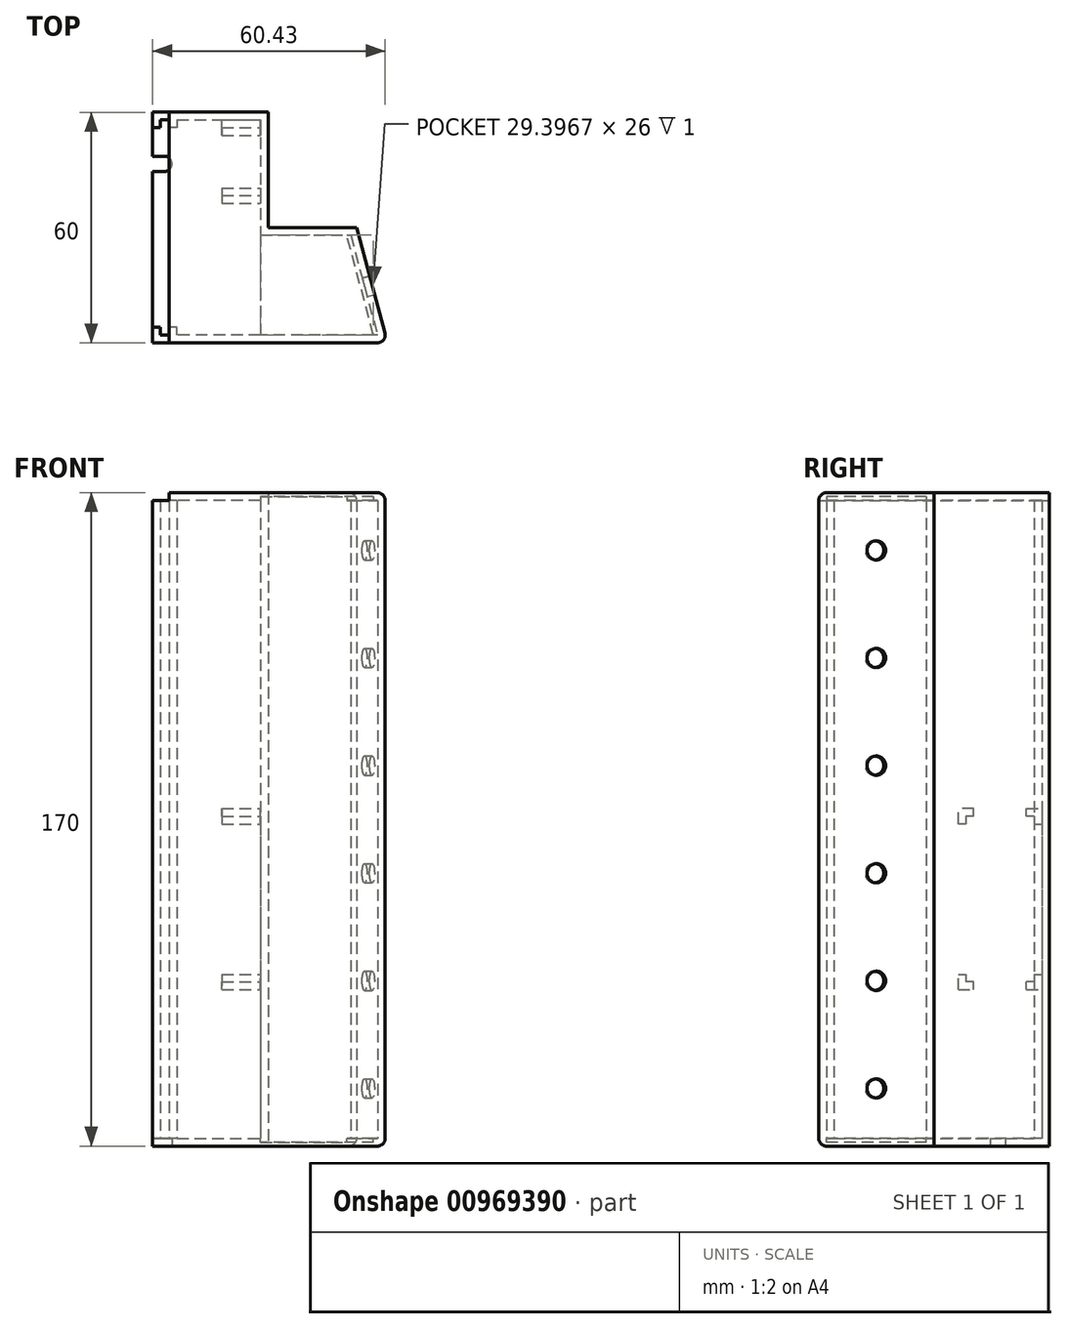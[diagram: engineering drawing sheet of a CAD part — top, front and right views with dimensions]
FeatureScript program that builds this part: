
annotation { "Feature Type Name" : "Feature", "Feature Type Description" : "" }
export const myFeature = defineFeature(function(context is Context, id is Id, definition is map)
    precondition{}
    {
        {
            var Q0;
            Q0=qCreatedBy(makeId("Top.planeOp"),FACE);
            var sketch = newSketch(context, id + "F0", { "sketchPlane" : qUnion([Q0])});
            skLineSegment(sketch, "E0.bottom", {"start": v(18.2, -39.79) * mm, "end": v(-42.84, -39.79) * mm});
            skLineSegment(sketch, "E0.right", {"start": v(-42.84, -39.79) * mm, "end": v(-42.84, -9.79) * mm});
            skLineSegment(sketch, "E1.top", {"start": v(-42.84, 20.21) * mm, "end": v(-12.84, 20.21) * mm});
            skLineSegment(sketch, "E1.left", {"start": v(-42.84, -9.79) * mm, "end": v(-42.84, 20.21) * mm});
            skLineSegment(sketch, "E1.right", {"start": v(-12.84, -9.79) * mm, "end": v(-12.84, 20.21) * mm});
            skLineSegment(sketch, "E2", {"start": v(10.16, -9.79) * mm, "end": v(18.2, -39.79) * mm});
            skLineSegment(sketch, "E3", {"start": v(10.16, -9.79) * mm, "end": v(10.16, -39.79) * mm, "construction": true});
            skLineSegment(sketch, "E4", {"start": v(-12.84, -9.79) * mm, "end": v(10.16, -9.79) * mm});
            skSolve(sketch);
        }
        {
            var Q0;
            Q0=makeQuery(id+"F0.imprint","IMPRINT",FACE,{"disambiguationData":[TD([[makeQuery(id+"F0.imprint","IMPRINT",EDGE,{"derivedFrom":sQuery(id+"F0.wireOp",EDGE,"E0.bottom")}),-1.0]])]});
            extrude(context, id + "F1", {"entities" : qUnion([Q0]), "depth" : 2 * mm, "offsetDistance" : 25 * mm});
        }
        {
            var Q0;
            Q0=makeQuery(id+"F1.opExtrude","CAP_FACE",FACE,{"disambiguationData":[OSD([sQuery(id+"F0.wireOp",EDGE,"E0.bottom"),sQuery(id+"F0.wireOp",EDGE,"E0.right"),sQuery(id+"F0.wireOp",EDGE,"E1.top"),sQuery(id+"F0.wireOp",EDGE,"E1.left"),sQuery(id+"F0.wireOp",EDGE,"E1.right"),sQuery(id+"F0.wireOp",EDGE,"E2"),sQuery(id+"F0.wireOp",EDGE,"E4")])],"isStart":false});
            var sketch = newSketch(context, id + "F2", { "sketchPlane" : qUnion([Q0])});
            skLineSegment(sketch, "E5", {"start": v(-36.54, 18.21) * mm, "end": v(-14.84, 18.21) * mm});
            skLineSegment(sketch, "E6", {"start": v(-14.84, 18.21) * mm, "end": v(-14.84, -11.79) * mm});
            skLineSegment(sketch, "E7", {"start": v(-14.84, -11.79) * mm, "end": v(8.63, -11.79) * mm});
            skLineSegment(sketch, "E8", {"start": v(8.63, -11.79) * mm, "end": v(15.6, -37.79) * mm});
            skLineSegment(sketch, "E9", {"start": v(15.6, -37.79) * mm, "end": v(-36.54, -37.79) * mm});
            skLineSegment(sketch, "E10", {"start": v(-36.54, 18.21) * mm, "end": v(-36.54, 16.21) * mm});
            skLineSegment(sketch, "E11", {"start": v(-36.54, 16.21) * mm, "end": v(-38.54, 16.21) * mm});
            skLineSegment(sketch, "E12", {"start": v(-38.54, 16.21) * mm, "end": v(-38.54, 18.21) * mm});
            skLineSegment(sketch, "E13", {"start": v(-38.54, 18.21) * mm, "end": v(-40.84, 18.21) * mm});
            skLineSegment(sketch, "E14", {"start": v(-40.84, 18.21) * mm, "end": v(-40.84, 16.21) * mm});
            skLineSegment(sketch, "E15", {"start": v(-40.84, 16.21) * mm, "end": v(-42.84, 16.21) * mm});
            skLineSegment(sketch, "E16", {"start": v(-36.54, -37.79) * mm, "end": v(-36.54, -35.79) * mm});
            skLineSegment(sketch, "E17", {"start": v(-36.54, -35.79) * mm, "end": v(-38.54, -35.79) * mm});
            skLineSegment(sketch, "E18", {"start": v(-38.54, -35.79) * mm, "end": v(-38.54, -37.79) * mm});
            skLineSegment(sketch, "E19", {"start": v(-38.54, -37.79) * mm, "end": v(-40.84, -37.79) * mm});
            skLineSegment(sketch, "E20", {"start": v(-40.84, -37.79) * mm, "end": v(-40.84, -35.79) * mm});
            skLineSegment(sketch, "E21", {"start": v(-40.84, -35.79) * mm, "end": v(-42.84, -35.79) * mm});
            skSolve(sketch);
        }
        {
            var Q0;
            Q0=makeQuery(id+"F2.imprint","IMPRINT",FACE,{"disambiguationData":[TD([[makeQuery(id+"F2.imprint","IMPRINT",EDGE,{"derivedFrom":sQuery(id+"F2.wireOp",EDGE,"E5")}),1.0]])]});
            extrude(context, id + "F3", {"entities" : qUnion([Q0]), "operationType" : NewBodyOperationType.ADD, "depth" : 166 * mm, "offsetDistance" : 25 * mm});
        }
        {
            var Q0;
            {var subQ0=sQuery(id+"F0.wireOp",EDGE,"E2");Q0=makeQuery(id+"F3.boolean.opBoolean","MERGE",FACE,{"derivedFrom":[makeQuery(id+"F1.opExtrude","SWEPT_FACE",FACE,{"disambiguationData":[OSD([subQ0])]}),makeQuery(id+"F3.opExtrude","SWEPT_FACE",FACE,{"disambiguationData":[OSD([subQ0])]})]});}
            var sketch = newSketch(context, id + "F4", { "sketchPlane" : qUnion([Q0])});
            skLineSegment(sketch, "E22", {"start": v(-27.61, 168) * mm, "end": v(-27.61, 0) * mm, "construction": true});
            skPoint(sketch, "E23", {"position": v(-27.61, 155) * mm});
            skPoint(sketch, "E24", {"position": v(-27.61, 127) * mm});
            skPoint(sketch, "E25", {"position": v(-27.61, 99) * mm});
            skPoint(sketch, "E26", {"position": v(-27.61, 71) * mm});
            skPoint(sketch, "E27", {"position": v(-27.61, 43) * mm});
            skPoint(sketch, "E28", {"position": v(-27.61, 15) * mm});
            skSolve(sketch);
        }
        {
            var Q0;
            Q0=sQuery(id+"F4.wireOp",VERTEX,"E23");
            var Q1;
            Q1=sQuery(id+"F4.wireOp",VERTEX,"E24");
            var Q2;
            Q2=sQuery(id+"F4.wireOp",VERTEX,"E25");
            var Q3;
            Q3=sQuery(id+"F4.wireOp",VERTEX,"E26");
            var Q4;
            Q4=sQuery(id+"F4.wireOp",VERTEX,"E27");
            var Q5;
            Q5=sQuery(id+"F4.wireOp",VERTEX,"E28");
            var Q6;
            Q6=makeQuery(id+"F1.opExtrude","SWEPT_BODY",BODY,{"disambiguationData":[OSD([sQuery(id+"F0.wireOp",EDGE,"E0.bottom"),sQuery(id+"F0.wireOp",EDGE,"E0.right"),sQuery(id+"F0.wireOp",EDGE,"E1.top"),sQuery(id+"F0.wireOp",EDGE,"E1.left"),sQuery(id+"F0.wireOp",EDGE,"E1.right"),sQuery(id+"F0.wireOp",EDGE,"E2"),sQuery(id+"F0.wireOp",EDGE,"E4")])]});
            hole(context, id + "F5", {"style" : HoleStyle.SIMPLE, "endStyle" : HoleEndStyle.BLIND, "holeDiameter" : 5 * mm, "majorDiameter" : 5 * mm, "holeDepth" : 10 * mm, "isTappedThrough" : true, "tappedDepth" : 12 * mm, "tapClearance" : 3, "locations" : qUnion([Q0, Q1, Q2, Q3, Q4, Q5]), "scope" : qUnion([Q6])});
        }
        {
            var Q0;
            Q0=makeQuery(id+"F3.opExtrude","CAP_FACE",FACE,{"disambiguationData":[OSD([sQuery(id+"F0.wireOp",EDGE,"E0.bottom"),sQuery(id+"F0.wireOp",EDGE,"E0.right"),sQuery(id+"F0.wireOp",EDGE,"E1.top"),sQuery(id+"F0.wireOp",EDGE,"E1.left"),sQuery(id+"F0.wireOp",EDGE,"E1.right"),sQuery(id+"F0.wireOp",EDGE,"E2"),sQuery(id+"F0.wireOp",EDGE,"E4"),sQuery(id+"F2.wireOp",EDGE,"E5"),sQuery(id+"F2.wireOp",EDGE,"E6"),sQuery(id+"F2.wireOp",EDGE,"E7"),sQuery(id+"F2.wireOp",EDGE,"E8"),sQuery(id+"F2.wireOp",EDGE,"E9"),sQuery(id+"F2.wireOp",EDGE,"E10"),sQuery(id+"F2.wireOp",EDGE,"E11"),sQuery(id+"F2.wireOp",EDGE,"E12"),sQuery(id+"F2.wireOp",EDGE,"E13"),sQuery(id+"F2.wireOp",EDGE,"E14"),sQuery(id+"F2.wireOp",EDGE,"E15"),sQuery(id+"F2.wireOp",EDGE,"E16"),sQuery(id+"F2.wireOp",EDGE,"E17"),sQuery(id+"F2.wireOp",EDGE,"E18"),sQuery(id+"F2.wireOp",EDGE,"E19"),sQuery(id+"F2.wireOp",EDGE,"E20"),sQuery(id+"F2.wireOp",EDGE,"E21")])],"isStart":false});
            var sketch = newSketch(context, id + "F6", { "sketchPlane" : qUnion([Q0])});
            skLineSegment(sketch, "E29", {"start": v(18.2, -39.79) * mm, "end": v(-38.54, -39.79) * mm});
            skLineSegment(sketch, "E30", {"start": v(-38.54, -39.79) * mm, "end": v(-38.54, -37.79) * mm});
            skLineSegment(sketch, "E31", {"start": v(-38.54, -37.79) * mm, "end": v(-38.54, 20.21) * mm});
            skLineSegment(sketch, "E32", {"start": v(-38.54, 20.21) * mm, "end": v(-12.84, 20.21) * mm});
            skLineSegment(sketch, "E33", {"start": v(-12.84, 20.21) * mm, "end": v(-12.84, -9.79) * mm});
            skLineSegment(sketch, "E34", {"start": v(-12.84, -9.79) * mm, "end": v(10.16, -9.79) * mm});
            skLineSegment(sketch, "E35", {"start": v(10.16, -9.79) * mm, "end": v(18.2, -39.79) * mm});
            skSolve(sketch);
        }
        {
            var Q0;
            Q0=makeQuery(id+"F6.imprint","IMPRINT",FACE,{"disambiguationData":[TD([[makeQuery(id+"F6.imprint","IMPRINT",EDGE,{"derivedFrom":makeQuery(id+"F3.opExtrude","CAP_EDGE",EDGE,{"disambiguationData":[OSD([sQuery(id+"F2.wireOp",EDGE,"E5")])],"isStart":false})}),-1.0]])]});
            var Q1;
            Q1=makeQuery(id+"F6.imprint","IMPRINT",FACE,{"disambiguationData":[TD([[makeQuery(id+"F6.imprint","IMPRINT",EDGE,{"derivedFrom":sQuery(id+"F6.wireOp",EDGE,"E29")}),-1.0]])]});
            extrude(context, id + "F7", {"entities" : qUnion([Q0, Q1]), "operationType" : NewBodyOperationType.ADD, "depth" : 2 * mm, "offsetDistance" : 25 * mm});
        }
        {
            var Q0;
            Q0=makeQuery(id+"F1.opExtrude","CAP_EDGE",EDGE,{"disambiguationData":[OSD([sQuery(id+"F0.wireOp",EDGE,"E0.bottom")])],"isStart":true});
            var Q1;
            {var subQ0=sQuery(id+"F0.wireOp",EDGE,"E2");var subQ1=sQuery(id+"F0.wireOp",EDGE,"E0.bottom");Q1=makeQuery(id+"F7.boolean.opBoolean","MERGE",EDGE,{"derivedFrom":[makeQuery(id+"F3.boolean.opBoolean","MERGE",EDGE,{"derivedFrom":[makeQuery(id+"F1.opExtrude","SWEPT_EDGE",EDGE,{"disambiguationData":[OSD([subQ1,subQ0])]}),makeQuery(id+"F3.opExtrude","SWEPT_EDGE",EDGE,{"disambiguationData":[OSD([subQ1,subQ0])]})]}),makeQuery(id+"F7.opExtrude","SWEPT_EDGE",EDGE,{"disambiguationData":[OSD([sQuery(id+"F6.wireOp",EDGE,"E29"),sQuery(id+"F6.wireOp",EDGE,"E35")])]})]});}
            var Q2;
            Q2=makeQuery(id+"F1.opExtrude","CAP_EDGE",EDGE,{"disambiguationData":[OSD([sQuery(id+"F0.wireOp",EDGE,"E2")])],"isStart":true});
            var Q3;
            Q3=makeQuery(id+"F7.opExtrude","CAP_EDGE",EDGE,{"disambiguationData":[OSD([sQuery(id+"F6.wireOp",EDGE,"E29")])],"isStart":false});
            var Q4;
            Q4=makeQuery(id+"F7.opExtrude","CAP_EDGE",EDGE,{"disambiguationData":[OSD([sQuery(id+"F6.wireOp",EDGE,"E35")])],"isStart":false});
            fillet(context, id + "F8", {"entities" : qUnion([Q0, Q1, Q2, Q3, Q4]), "radius" : 2 * mm, "tangentPropagation" : true, "allowEdgeOverflow" : false});
        }
        {
            var Q0;
            Q0=makeQuery(id+"F1.opExtrude","CAP_FACE",FACE,{"disambiguationData":[OSD([sQuery(id+"F0.wireOp",EDGE,"E0.bottom"),sQuery(id+"F0.wireOp",EDGE,"E0.right"),sQuery(id+"F0.wireOp",EDGE,"E1.top"),sQuery(id+"F0.wireOp",EDGE,"E1.left"),sQuery(id+"F0.wireOp",EDGE,"E1.right"),sQuery(id+"F0.wireOp",EDGE,"E2"),sQuery(id+"F0.wireOp",EDGE,"E4")])],"isStart":true});
            var sketch = newSketch(context, id + "F9", { "sketchPlane" : qUnion([Q0])});
            skPoint(sketch, "E36", {"position": v(-39.84, -6.78) * mm});
            skCircle(sketch, "E37", {"center": v(-39.84, -6.78) * mm, "radius": 2 * mm});
            skLineSegment(sketch, "E38", {"start": v(-39.84, -8.78) * mm, "end": v(-42.84, -8.78) * mm});
            skLineSegment(sketch, "E39", {"start": v(-39.84, -4.78) * mm, "end": v(-42.84, -4.78) * mm});
            skSolve(sketch);
        }
        {
            var Q0;
            {var subQ0=sQuery(id+"F9.wireOp",EDGE,"E37");var subQ1=makeQuery(id+"F9.imprint","INTERSECT",VERTEX,{"derivedFrom":[subQ0,sQuery(id+"F9.wireOp",EDGE,"E38")]});Q0=makeQuery(id+"F9.imprint","IMPRINT",FACE,{"disambiguationData":[TD([[makeQuery(id+"F9.imprint","IMPRINT",EDGE,{"disambiguationData":[TD([[subQ1,1.0]])],"derivedFrom":subQ0}),1.0]])]});}
            var Q1;
            {var subQ0=sQuery(id+"F9.wireOp",EDGE,"E38");Q1=makeQuery(id+"F9.imprint","IMPRINT",FACE,{"disambiguationData":[TD([[makeQuery(id+"F9.imprint","IMPRINT",EDGE,{"derivedFrom":subQ0}),-1.0]])]});}
            extrude(context, id + "F10", {"entities" : qUnion([Q0, Q1]), "operationType" : NewBodyOperationType.REMOVE, "oppositeDirection" : true, "depth" : 25 * mm, "offsetDistance" : 25 * mm});
        }
        {
            var Q0;
            Q0=makeQuery(id+"F3.opExtrude","SWEPT_FACE",FACE,{"disambiguationData":[OSD([sQuery(id+"F2.wireOp",EDGE,"E6")])]});
            var sketch = newSketch(context, id + "F11", { "sketchPlane" : qUnion([Q0])});
            skLineSegment(sketch, "E40.bottom", {"start": v(-16.21, 85.79) * mm, "end": v(1.49, 85.79) * mm});
            skLineSegment(sketch, "E40.top", {"start": v(-16.21, 42.69) * mm, "end": v(1.49, 42.69) * mm});
            skLineSegment(sketch, "E40.left", {"start": v(-16.21, 85.79) * mm, "end": v(-16.21, 42.69) * mm});
            skLineSegment(sketch, "E40.right", {"start": v(1.49, 85.79) * mm, "end": v(1.49, 42.69) * mm});
            skLineSegment(sketch, "E41.bottom", {"start": v(3.49, 40.69) * mm, "end": v(-0.51, 40.69) * mm});
            skLineSegment(sketch, "E41.top", {"start": v(3.49, 44.69) * mm, "end": v(-0.51, 44.69) * mm});
            skLineSegment(sketch, "E41.left", {"start": v(3.49, 40.69) * mm, "end": v(3.49, 44.69) * mm});
            skLineSegment(sketch, "E41.right", {"start": v(-0.51, 40.69) * mm, "end": v(-0.51, 44.69) * mm});
            skPoint(sketch, "E41.middle", {"position": v(1.49, 42.69) * mm});
            skLineSegment(sketch, "E42.bottom", {"start": v(-14.21, 40.69) * mm, "end": v(-18.21, 40.69) * mm});
            skLineSegment(sketch, "E42.top", {"start": v(-14.21, 44.69) * mm, "end": v(-18.21, 44.69) * mm});
            skLineSegment(sketch, "E42.left", {"start": v(-14.21, 40.69) * mm, "end": v(-14.21, 44.69) * mm});
            skLineSegment(sketch, "E42.right", {"start": v(-18.21, 40.69) * mm, "end": v(-18.21, 44.69) * mm});
            skPoint(sketch, "E42.middle", {"position": v(-16.21, 42.69) * mm});
            skLineSegment(sketch, "E43.bottom", {"start": v(-14.21, 83.79) * mm, "end": v(-18.21, 83.79) * mm});
            skLineSegment(sketch, "E43.top", {"start": v(-14.21, 87.79) * mm, "end": v(-18.21, 87.79) * mm});
            skLineSegment(sketch, "E43.left", {"start": v(-14.21, 83.79) * mm, "end": v(-14.21, 87.79) * mm});
            skLineSegment(sketch, "E43.right", {"start": v(-18.21, 83.79) * mm, "end": v(-18.21, 87.79) * mm});
            skPoint(sketch, "E43.middle", {"position": v(-16.21, 85.79) * mm});
            skLineSegment(sketch, "E44.bottom", {"start": v(-0.51, 83.79) * mm, "end": v(3.49, 83.79) * mm});
            skLineSegment(sketch, "E44.top", {"start": v(-0.51, 87.79) * mm, "end": v(3.49, 87.79) * mm});
            skLineSegment(sketch, "E44.left", {"start": v(-0.51, 83.79) * mm, "end": v(-0.51, 87.79) * mm});
            skLineSegment(sketch, "E44.right", {"start": v(3.49, 83.79) * mm, "end": v(3.49, 87.79) * mm});
            skPoint(sketch, "E44.middle", {"position": v(1.49, 85.79) * mm});
            skSolve(sketch);
        }
        {
            var Q0;
            {var subQ4=sQuery(id+"F11.wireOp",EDGE,"E41.bottom");Q0=makeQuery(id+"F11.imprint","IMPRINT",FACE,{"disambiguationData":[TD([[makeQuery(id+"F11.imprint","IMPRINT",EDGE,{"derivedFrom":subQ4}),-1.0]])]});}
            var Q1;
            {var subQ4=sQuery(id+"F11.wireOp",EDGE,"E42.bottom");Q1=makeQuery(id+"F11.imprint","IMPRINT",FACE,{"disambiguationData":[TD([[makeQuery(id+"F11.imprint","IMPRINT",EDGE,{"derivedFrom":subQ4}),-1.0]])]});}
            var Q2;
            {var subQ0=sQuery(id+"F11.wireOp",EDGE,"E43.top");Q2=makeQuery(id+"F11.imprint","IMPRINT",FACE,{"disambiguationData":[TD([[makeQuery(id+"F11.imprint","IMPRINT",EDGE,{"derivedFrom":subQ0}),1.0]])]});}
            var Q3;
            {var subQ6=sQuery(id+"F11.wireOp",EDGE,"E44.top");Q3=makeQuery(id+"F11.imprint","IMPRINT",FACE,{"disambiguationData":[TD([[makeQuery(id+"F11.imprint","IMPRINT",EDGE,{"derivedFrom":subQ6}),-1.0]])]});}
            extrude(context, id + "F12", {"entities" : qUnion([Q0, Q1, Q2, Q3]), "operationType" : NewBodyOperationType.ADD, "depth" : 10 * mm, "offsetDistance" : 25 * mm});
        }
        {
            var Q0;
            Q0=makeQuery(id+"F1.opExtrude","CAP_FACE",FACE,{"disambiguationData":[OSD([sQuery(id+"F0.wireOp",EDGE,"E0.bottom"),sQuery(id+"F0.wireOp",EDGE,"E0.right"),sQuery(id+"F0.wireOp",EDGE,"E1.top"),sQuery(id+"F0.wireOp",EDGE,"E1.left"),sQuery(id+"F0.wireOp",EDGE,"E1.right"),sQuery(id+"F0.wireOp",EDGE,"E2"),sQuery(id+"F0.wireOp",EDGE,"E4")])],"isStart":false});
            var sketch = newSketch(context, id + "F13", { "sketchPlane" : qUnion([Q0])});
            skLineSegment(sketch, "E45", {"start": v(7.6, -11.79) * mm, "end": v(-14.84, -11.79) * mm});
            skLineSegment(sketch, "E46", {"start": v(-14.84, -11.79) * mm, "end": v(-14.84, -37.79) * mm});
            skLineSegment(sketch, "E47", {"start": v(-14.84, -37.79) * mm, "end": v(14.56, -37.79) * mm});
            skLineSegment(sketch, "E48", {"start": v(14.56, -37.79) * mm, "end": v(7.6, -11.79) * mm});
            skSolve(sketch);
        }
        {
            var Q0;
            Q0=makeQuery(id+"F13.imprint","IMPRINT",FACE,{"disambiguationData":[TD([[makeQuery(id+"F13.imprint","IMPRINT",EDGE,{"derivedFrom":sQuery(id+"F13.wireOp",EDGE,"E45")}),-1.0]])]});
            extrude(context, id + "F14", {"entities" : qUnion([Q0]), "operationType" : NewBodyOperationType.REMOVE, "oppositeDirection" : true, "depth" : 1 * mm, "offsetDistance" : 25 * mm});
        }
        {
            var Q0;
            Q0=makeQuery(id+"F7.opExtrude","CAP_FACE",FACE,{"disambiguationData":[OSD([sQuery(id+"F6.wireOp",EDGE,"E29"),sQuery(id+"F6.wireOp",EDGE,"E30"),sQuery(id+"F6.wireOp",EDGE,"E31"),sQuery(id+"F6.wireOp",EDGE,"E32"),sQuery(id+"F6.wireOp",EDGE,"E33"),sQuery(id+"F6.wireOp",EDGE,"E34"),sQuery(id+"F6.wireOp",EDGE,"E35")])],"isStart":true});
            var sketch = newSketch(context, id + "F15", { "sketchPlane" : qUnion([Q0])});
            skLineSegment(sketch, "E49", {"start": v(7.6, 11.79) * mm, "end": v(-14.84, 11.79) * mm});
            skLineSegment(sketch, "E50", {"start": v(-14.84, 11.79) * mm, "end": v(-14.84, 37.79) * mm});
            skLineSegment(sketch, "E51", {"start": v(-14.84, 37.79) * mm, "end": v(14.56, 37.79) * mm});
            skLineSegment(sketch, "E52", {"start": v(14.56, 37.79) * mm, "end": v(7.6, 11.79) * mm});
            skSolve(sketch);
        }
        {
            var Q0;
            Q0=makeQuery(id+"F15.imprint","IMPRINT",FACE,{"disambiguationData":[TD([[makeQuery(id+"F15.imprint","IMPRINT",EDGE,{"derivedFrom":sQuery(id+"F15.wireOp",EDGE,"E49")}),1.0]])]});
            extrude(context, id + "F16", {"entities" : qUnion([Q0]), "operationType" : NewBodyOperationType.REMOVE, "oppositeDirection" : true, "depth" : 1 * mm, "offsetDistance" : 25 * mm});
        }
    });
